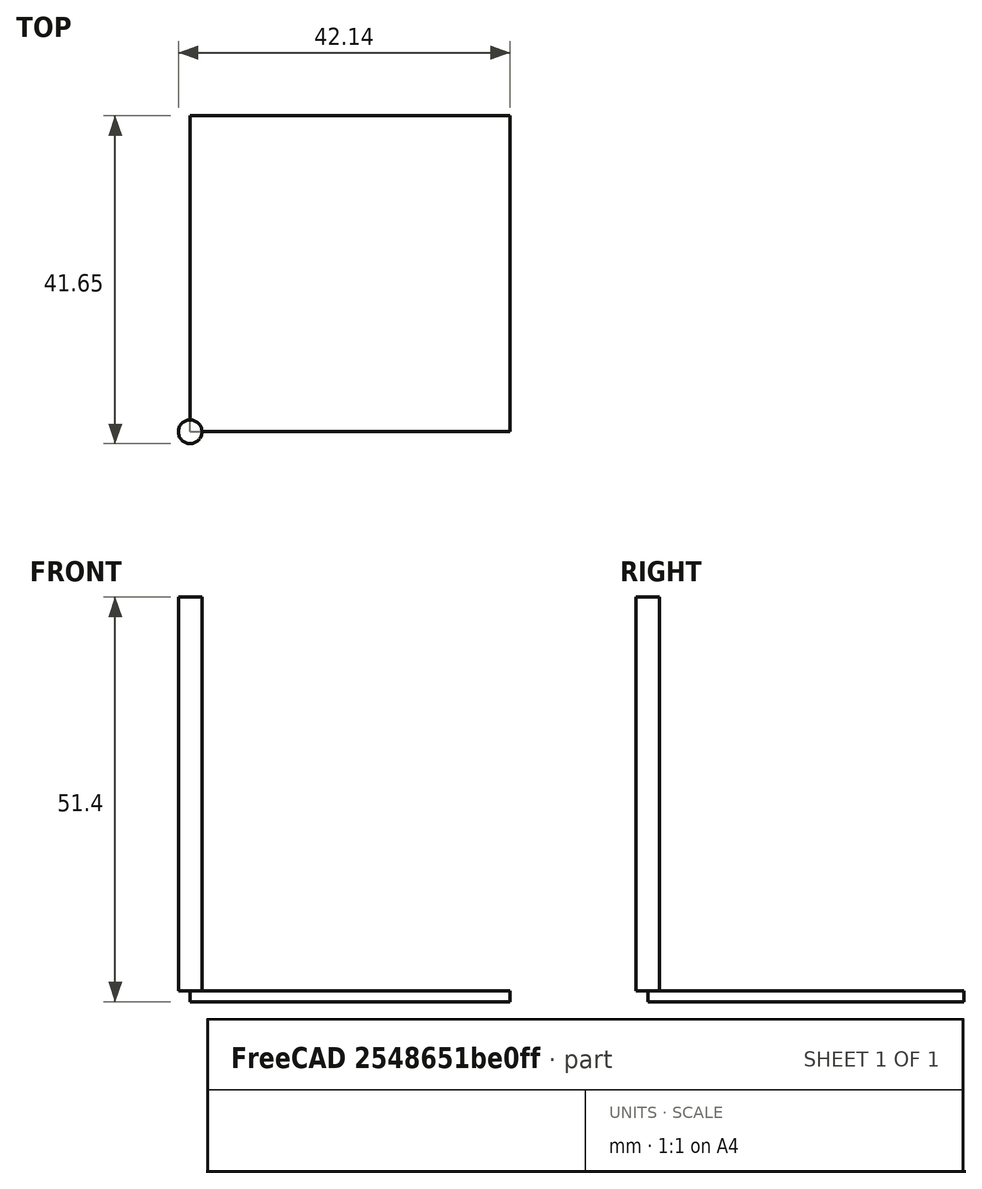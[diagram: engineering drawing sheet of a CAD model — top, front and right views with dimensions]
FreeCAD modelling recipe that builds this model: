
FCSTD DOCUMENT  (FreeCAD 0.19R24276 (Git))
Label: AdaptateurAlim2
License: All rights reserved
LicenseURL: http://en.wikipedia.org/wiki/All_rights_reserved
objects: Sketcher::SketchObject×5, PartDesign::Pocket×4, Path::FeaturePython×4, Part::FeaturePython×3, App::DocumentObjectGroup×2, PartDesign::Pad×1, PartDesign::Body×1, App::FeaturePython×1, Path::FeatureCompoundPython×1, Mesh::FeaturePython×1
note: 21 computed .brp shape members not serialized (recipe doc carries the construction recipe); baked Part::Feature solids carry a one-line shape summary decoded from their .brp

FEATURE [Sketcher::SketchObject] Sketch003
  FullyConstrained = false
  MapMode = 5
  Support = -> [XY_Plane002]
  sketch-geometry (8):
    g0: LineSegment StartX=5.69576 StartY=-19.8497 StartZ=0 EndX=35.4451 EndY=-19.8497 EndZ=0
    g1: LineSegment StartX=40.6035 StartY=-25.0081 StartZ=0 EndX=40.6035 EndY=-55.4325 EndZ=0
    g2: LineSegment StartX=36.036 StartY=-60 StartZ=0 EndX=4.83563 EndY=-60 EndZ=0
    g3: LineSegment StartX=-0.0353714 StartY=-55.129 StartZ=0 EndX=-0.0353714 EndY=-25.5808 EndZ=0
    g4: ArcOfCircle CenterX=5.69576 CenterY=-25.5808 CenterZ=0 NormalX=0 NormalY=0 NormalZ=1 AngleXU=0 Radius=5.73113 StartAngle=1.5708 EndAngle=3.14159
    g5: ArcOfCircle CenterX=35.4451 CenterY=-25.0081 CenterZ=0 NormalX=0 NormalY=0 NormalZ=1 AngleXU=0 Radius=5.1584 StartAngle=2e-16 EndAngle=1.5708
    g6: ArcOfCircle CenterX=36.036 CenterY=-55.4325 CenterZ=0 NormalX=0 NormalY=0 NormalZ=1 AngleXU=0 Radius=4.56749 StartAngle=4.71239 EndAngle=6.28319
    g7: ArcOfCircle CenterX=4.83563 CenterY=-55.129 CenterZ=0 NormalX=0 NormalY=0 NormalZ=1 AngleXU=0 Radius=4.871 StartAngle=3.14159 EndAngle=4.71239
  constraints (12):
    c: Horizontal(g0)
    c: Horizontal(g2)
    c: Vertical(g1)
    c: Vertical(g3)
    c: Tangent(g0,g4) = 1.5708
    c: Tangent(g3,g4) = 1.5708
    c: Tangent(g0,g5) = 1.5708
    c: Tangent(g1,g5) = 1.5708
    c: Tangent(g1,g6) = 1.5708
    c: Tangent(g2,g6) = 1.5708
    c: Tangent(g2,g7) = 1.5708
    c: Tangent(g3,g7) = 1.5708
FEATURE [PartDesign::Pad] Pad002
  Direction = (1,1,1)
  Length = 1.4
  Length2 = 100
  Profile = -> Sketch003
  Type = 0
FEATURE [Sketcher::SketchObject] Sketch004  label="Trous fiches mâles"
  FullyConstrained = false
  MapMode = 5
  Placement = pos=(0,0,1.4) rot=(0,0,1;0rad)
  Support = -> [Pad002]
  sketch-geometry (2):
    g0: Circle CenterX=22 CenterY=-49.3448 CenterZ=0 NormalX=0 NormalY=0 NormalZ=1 AngleXU=0 Radius=3
    g1: Circle CenterX=22 CenterY=-30.3448 CenterZ=0 NormalX=0 NormalY=0 NormalZ=1 AngleXU=0 Radius=3
  constraints (5):
    c: DistanceX(g-1,g1) = 22
    c: DistanceX(g-1,g0) = 22
    c: DistanceY(g0,g1) = 19
    c: Diameter(g1) = 6
    c: Diameter(g0) = 6
FEATURE [PartDesign::Pocket] Pocket001  label="fiches mâles"
  BaseFeature = -> Pad002
  Length = 5
  Length2 = 100
  Profile = -> Sketch004
  Type = 1
FEATURE [Sketcher::SketchObject] Sketch006  label="Trous fiches femelles"
  FullyConstrained = false
  MapMode = 5
  Placement = pos=(0,0,1.4) rot=(0,0,1;0rad)
  Support = -> [Pocket001]
  sketch-geometry (2):
    g0: Circle CenterX=10 CenterY=-40.1651 CenterZ=0 NormalX=0 NormalY=0 NormalZ=1 AngleXU=0 Radius=3
    g1: Circle CenterX=29 CenterY=-39.9952 CenterZ=0 NormalX=0 NormalY=0 NormalZ=1 AngleXU=0 Radius=3
  constraints (4):
    c: Diameter(g1) = 6
    c: Diameter(g0) = 6
    c: DistanceX(g0,g1) = 19
    c: DistanceX(g-1,g0) = 10
FEATURE [PartDesign::Pocket] Pocket002  label="fiches femelles"
  BaseFeature = -> Pocket001
  Length = 5
  Length2 = 100
  Profile = -> Sketch006
  Type = 1
FEATURE [Sketcher::SketchObject] Sketch007
  FullyConstrained = false
  MapMode = 5
  Placement = pos=(0,0,1.4) rot=(0,0,1;0rad)
  Support = -> [Pocket002]
  sketch-geometry (2):
    g0: Circle CenterX=33 CenterY=-27 CenterZ=0 NormalX=0 NormalY=0 NormalZ=1 AngleXU=0 Radius=3.5
    g1: LineSegment StartX=-10 StartY=-20 StartZ=0 EndX=50 EndY=-20 EndZ=0
  constraints (4):
    c: Diameter(g0) = 7
    c: Horizontal(g1)
    c: DistanceY(g0) = -27
    c: DistanceX(g0) = 33
FEATURE [PartDesign::Pocket] Pocket003  label="interrupteur"
  BaseFeature = -> Pocket002
  Length = 5
  Length2 = 100
  Profile = -> Sketch007
  Type = 1
FEATURE [Sketcher::SketchObject] Sketch008
  FullyConstrained = true
  MapMode = 5
  Placement = pos=(0,0,1.4) rot=(0,0,1;0rad)
  Support = -> [Pocket003]
  sketch-geometry (1):
    g0: Circle CenterX=10 CenterY=-27 CenterZ=0 NormalX=0 NormalY=0 NormalZ=1 AngleXU=0 Radius=3.25
  constraints (3):
    c: Diameter(g0) = 6.5
    c: DistanceX(g-1,g0) = 10
    c: DistanceY(g0) = -27
FEATURE [PartDesign::Pocket] Pocket004  label="LED"
  BaseFeature = -> Pocket003
  Length = 5
  Length2 = 100
  Profile = -> Sketch008
  Type = 1
FEATURE [PartDesign::Body] Body002
  Group = -> [Sketch003,Pad002,Sketch004,Pocket001,Sketch006,Pocket002,Sketch007,Pocket003,Sketch008,Pocket004]
  Origin = -> Origin002
  Placement = pos=(0,122,0) rot=(0,0,1;0rad)
  Tip = -> Pocket004
FEATURE [App::FeaturePython] SetupSheet  # Path/CAM operation (typed FeaturePython)
  ClearanceHeightExpression = OpStockZMax+SetupSheet.ClearanceHeightOffset
  ClearanceHeightOffset = 5
  CoolantMode = 0
  CoolantModes = None | Flood | Mist
  FinalDepthExpression = OpFinalDepth
  HorizRapid = 0
  SafeHeightExpression = OpStockZMax+SetupSheet.SafeHeightOffset
  SafeHeightOffset = 3
  StartDepthExpression = OpStartDepth
  StepDownExpression = OpToolDiameter
  VertRapid = 0
FEATURE [Part::FeaturePython] Clone  label="Model-Body002"  # Draft clone (typed FeaturePython)
  AttacherType = Attacher::AttachEngine3D
  Fuse = false
  Objects = -> [Body002]
  PathResource = Model
  Placement = pos=(0.0353714,60,-1.4) rot=(0,0,1;0rad)
  Scale = (1,1,1)
FEATURE [App::DocumentObjectGroup] Model
  Group = -> [Clone]
FEATURE [Part::FeaturePython] ToolBit  label="Endmill"  # Path/CAM toolbit (typed FeaturePython)
  BitPropertyNames = Chipload | CuttingEdgeHeight | Diameter | Flutes | Length | Material | ShankDiameter
  BitShape = /Volumes/SSD/Applications/FreeCAD_0.19-24276.app/Contents/Resources/Mod/Path/Tools/Shape/endmill.fcstd
  Chipload = 0
  CuttingEdgeHeight = 30
  Diameter = 3
  Flutes = 0
  Length = 50
  Material = 0
  ShankDiameter = 3
  ShapeName = endmill
FEATURE [Path::FeaturePython] TC__Default_Tool  label="TC: Default Tool"  # Path/CAM operation (typed FeaturePython)
  HorizFeed = 0
  HorizRapid = 0
  SpindleDir = 0
  SpindleSpeed = 0
  Tool = -> ToolBit
  ToolNumber = 1
  VertFeed = 0
  VertRapid = 0
  expr: HorizRapid = SetupSheet.HorizRapid
  expr: VertRapid = SetupSheet.VertRapid
FEATURE [App::DocumentObjectGroup] Tools
  Group = -> [TC__Default_Tool]
FEATURE [Part::FeaturePython] Stock  # WARN: FeaturePython — macro-defined, semantics opaque (R4)
  Base = -> Model
  ExtXneg = 0
  ExtXpos = 0
  ExtYneg = 0
  ExtYpos = 0
  ExtZneg = 0
  ExtZpos = 0
  Placement = pos=(0,0,-1.4) rot=(0,0,1;0rad)
  StockType = FromBase
FEATURE [Path::FeaturePython] Pocket_Shape  # Path/CAM operation (typed FeaturePython)
  Active = true
  AreaParams:
    Tolerance = 1e-07
    FitArcs = True
    Simplify = False
    CleanDistance = 0.0
    Accuracy = 0.01
    Unit = 1.0
    MinArcPoints = 4
    MaxArcPoints = 100
    ClipperScale = 10000000.0
    Fill = 0
    Coplanar = 0
    Reorient = True
    Outline = False
    Explode = False
    OpenMode = 0
    Deflection = 0.01
    SubjectFill = 0
    ClipFill = 0
    Offset = 0.0
    ExtraPass = 0
    Stepover = 0.0
    LastStepover = 0.0
    JoinType = 0
    EndType = 0
    MiterLimit = 2.0
    RoundPrecision = 0.0
    PocketMode = 4
    ToolRadius = 1.5
    PocketExtraOffset = 0.0
    PocketStepover = 3.0
    PocketLastStepover = 0.0
    FromCenter = True
    Angle = 45.0
    AngleShift = 0.0
    Shift = 0.0
    Thicken = False
    SectionCount = -1
    Stepdown = 1.0
    SectionOffset = 0.0
    SectionTolerance = 1e-06
    SectionMode = 2
    Project = False
  AttemptInverseAngle = true
  Base = -> [Clone]
  ClearanceHeight = 5
  CoolantMode = None
  CutMode = 0
  CycleTime = Erreur de temps de cycle
  EnableRotation = 0
  ExtensionCorners = true
  ExtensionLengthDefault = 1.5
  ExtraOffset = 0
  FinalDepth = -1.4
  FinishDepth = 0
  InverseAngle = false
  KeepToolDown = false
  LimitDepthToFace = true
  MinTravel = false
  OffsetPattern = 3
  OpFinalDepth = -1.4
  OpStartDepth = 0
  OpStockZMax = 0
  OpStockZMin = -1.4
  OpToolDiameter = 3
  PathParams = {'orientation': 1, 'feedrate': 0.0, 'feedrate_v': 0.0, 'verbose': True, 'resume_height': 3.0, 'retraction': 5.0, 'return_end': True, 'preamble': False, 'start': Vector (22.781819747254715, 11.950911926255168, 5.0)}
  ReverseDirection = false
  SafeHeight = 3
  StartAt = 0
  StartDepth = 0
  StartPoint = (0,0,0)
  StepDown = 1.4
  StepOver = 100
  ToolController = -> TC__Default_Tool
  UseOutline = false
  UseStartPoint = false
  ZigZagAngle = 45
  expr: ExtensionLengthDefault = OpToolDiameter / 2
  expr: ClearanceHeight = OpStockZMax + SetupSheet.ClearanceHeightOffset
  expr: SafeHeight = OpStockZMax + SetupSheet.SafeHeightOffset
  expr: StepDown = 1.4
  expr: FinalDepth = -1.4
  expr: StartDepth = 0
FEATURE [Path::FeaturePython] Profile001  # Path/CAM operation (typed FeaturePython)
  Active = true
  AreaParams:
    Tolerance = 1e-07
    FitArcs = True
    Simplify = False
    CleanDistance = 0.0
    Accuracy = 0.01
    Unit = 1.0
    MinArcPoints = 4
    MaxArcPoints = 100
    ClipperScale = 10000000.0
    Fill = 0
    Coplanar = 0
    Reorient = True
    Outline = False
    Explode = False
    OpenMode = 0
    Deflection = 0.01
    SubjectFill = 0
    ClipFill = 0
    Offset = 1.5
    ExtraPass = 0
    Stepover = 0.0
    LastStepover = 0.0
    JoinType = 0
    EndType = 0
    MiterLimit = 2.0
    RoundPrecision = 0.0
    PocketMode = 0
    ToolRadius = 1.0
    PocketExtraOffset = 0.0
    PocketStepover = 0.0
    PocketLastStepover = 0.0
    FromCenter = False
    Angle = 45.0
    AngleShift = 0.0
    Shift = 0.0
    Thicken = False
    SectionCount = -1
    Stepdown = 1.0
    SectionOffset = 0.0
    SectionTolerance = 1e-06
    SectionMode = 2
    Project = False
  AttemptInverseAngle = true
  Base = -> [Clone]
  ClearanceHeight = 5
  CoolantMode = None
  CycleTime = Erreur de temps de cycle
  Direction = 0
  EnableRotation = 0
  FinalDepth = -1.4
  HandleMultipleFeatures = 0
  InverseAngle = false
  JoinType = 0
  LimitDepthToFace = true
  MiterLimit = 0.1
  OffsetExtra = 0
  OpFinalDepth = -1.4
  OpStartDepth = 0
  OpStockZMax = 0
  OpStockZMin = -1.4
  OpToolDiameter = 3
  PathParams = {'orientation': 1, 'feedrate': 0.0, 'feedrate_v': 0.0, 'verbose': True, 'resume_height': 3.0, 'retraction': 5.0, 'return_end': True, 'preamble': False}
  ReverseDirection = false
  SafeHeight = 3
  Side = 0
  StartDepth = 0
  StartPoint = (0,0,0)
  StepDown = 3
  ToolController = -> TC__Default_Tool
  UseComp = true
  UseStartPoint = false
  processCircles = false
  processHoles = false
  processPerimeter = true
  expr: ClearanceHeight = OpStockZMax + SetupSheet.ClearanceHeightOffset
  expr: SafeHeight = OpStockZMax + SetupSheet.SafeHeightOffset
  expr: StepDown = OpToolDiameter
  expr: FinalDepth = OpFinalDepth
  expr: StartDepth = OpStartDepth
FEATURE [Path::FeatureCompoundPython] Operations  # Path/CAM operation (typed FeaturePython)
  Group = -> [Pocket_Shape,Profile001]
  UsePlacements = false
FEATURE [Path::FeaturePython] Job  # Path/CAM operation (typed FeaturePython)
  CycleTime = 00:00:00
  Fixtures = G54
  GeometryTolerance = 0.01
  LastPostProcessDate = 2021-05-11 22:12:33.430457
  LastPostProcessOutput = /Volumes/SSD/Dev/CNC/MiscCNC/AdaptateurAlim2.gcode
  Model = -> Model
  Operations = -> Operations
  OrderOutputBy = 0
  PostProcessor = 1
  PostProcessorOutputFile = /Volumes/SSD/Dev/CNC/MiscCNC/AdaptateurAlim2.gcode
  SetupSheet = -> SetupSheet
  SplitOutput = false
  Stock = -> Stock
  Tools = -> Tools
FEATURE [Mesh::FeaturePython] CutMaterial  # WARN: FeaturePython — macro-defined, semantics opaque (R4)
